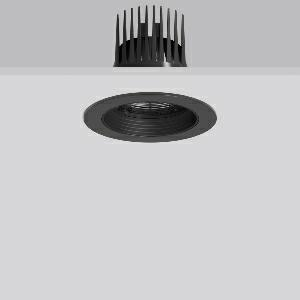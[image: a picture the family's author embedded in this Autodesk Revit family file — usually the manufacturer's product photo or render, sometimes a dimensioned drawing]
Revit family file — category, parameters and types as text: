
# Revit family: heledon_maxi_e_901761_003_3_b24e
name_source: partatom
category: Lighting Fixtures
units: mm (PartAtom-declared; Revit-internal decimal feet)

## family parameters
Cut with Voids When Loaded = No
Host = Face
Light Source = No
Part Type = Normal
Room Calculation Point = No
Round Connector Dimension = Use Diameter
Shared = No

## types (1)
- HELEDON maxi E (1 x LED Modul 935, 2800 lm, 3500)
    Apparent Load = 25 VA
    Approval mark = CE
    CIE Flux Codes = 96 100 100 100 100
    Color Rendering = 92
    Color Temperature = 3500
    Default Elevation = 1800 mm
    Description = Series: HELEDON maxi
Round recessed downlight. Housing: die-cast aluminium, powder-coated. Black plastic ring and recessed LED to prevent glare from the side. Optical assembly with lens made of plastic (polycarbonate) for the best homogeneous light distribution - can be changed without tools. Best colour rendering index Ra>90. Suitable for Recessed ceiling mounting. Installation without tools thanks to spring fastening system. Including separate LED converter with connecting cable 600 mm.High quality converter without flickering and stroboscopic effect. Through-wiring box (5 pole) available as accessory. The following accessories can be mounted without use of tools: interchangeable lenses, decorative glasses, honeycomb louvre, clear and frosted diffusers, white interchangeable plastic ring. 
Colour: deep black, matt (RAL 9005)
Diameter: 162 mm
Height: 3 mm
Cut-out diameter: 152 mm
Recess height: 200 mm
Luminaire: recess height: 135 mm
Lamp: LED
Socket: without socket
Colour temperature: 3500K
Colour rendering index (CRI): 92
System power: 25 W
Rated luminous flux: 2800 lm
Luminous efficiency: 112 lm/W
Control gear: Regulated power supply
Protection class: II
Type of protection: IP 20
    Height = 0 mm  [stored 0 ft]
    Lamp = 1 x LED Modul 935
    Lamp Light Flux = 2800 lm
    Lamp count = 1
    Length = 162 mm
    Lifetime = 50000 h
    Luminous efficacy = 112 lm/W
    Manufacturer = RZB
    ModVariant = No
    Model = 901761.003.3
    Mounting Place = Ceiling
    Mounting Type = Recessed
    Number of Poles = 1
    OnlyDefault = Yes
    Power Factor = 1
    Product Name = HELEDON maxi E
    Product group = Recessed downlights
    ProductGroupID = 402
    Protection Class = Protection class II
    Protection Degree = IP 20
    RLX_Detail_Level = 1
    RLX_Emergency_Light_Flux = 0 lm
    RLX_Emergency_Type = 0
    RLX_Emergency_Type_DB = No
    RlxData = <blob elided: 119901 chars, md5=dc0eac85>
    Socket = socket
    Standby Power = 0 W
    System Light Flux = 2800 lm
    System Power = 25 W
    Type Comments = Product without accessories
    Type Image = 901663.003.jpg
    URL = http://relux.com
    VarID = ---
    Voltage = 230 V
    Voltage Range = 220-240 V
    Weight = 0.00 kg
    Width = 0 mm  [stored 0 ft]

note: [stored X ft] marks values corroborated as IEEE doubles in the binary element streams (Revit-internal decimal feet)

## geometry (parser evidence)
native form markers: Blend x4, Sweep x11
no freeform markers — native parametric forms only
